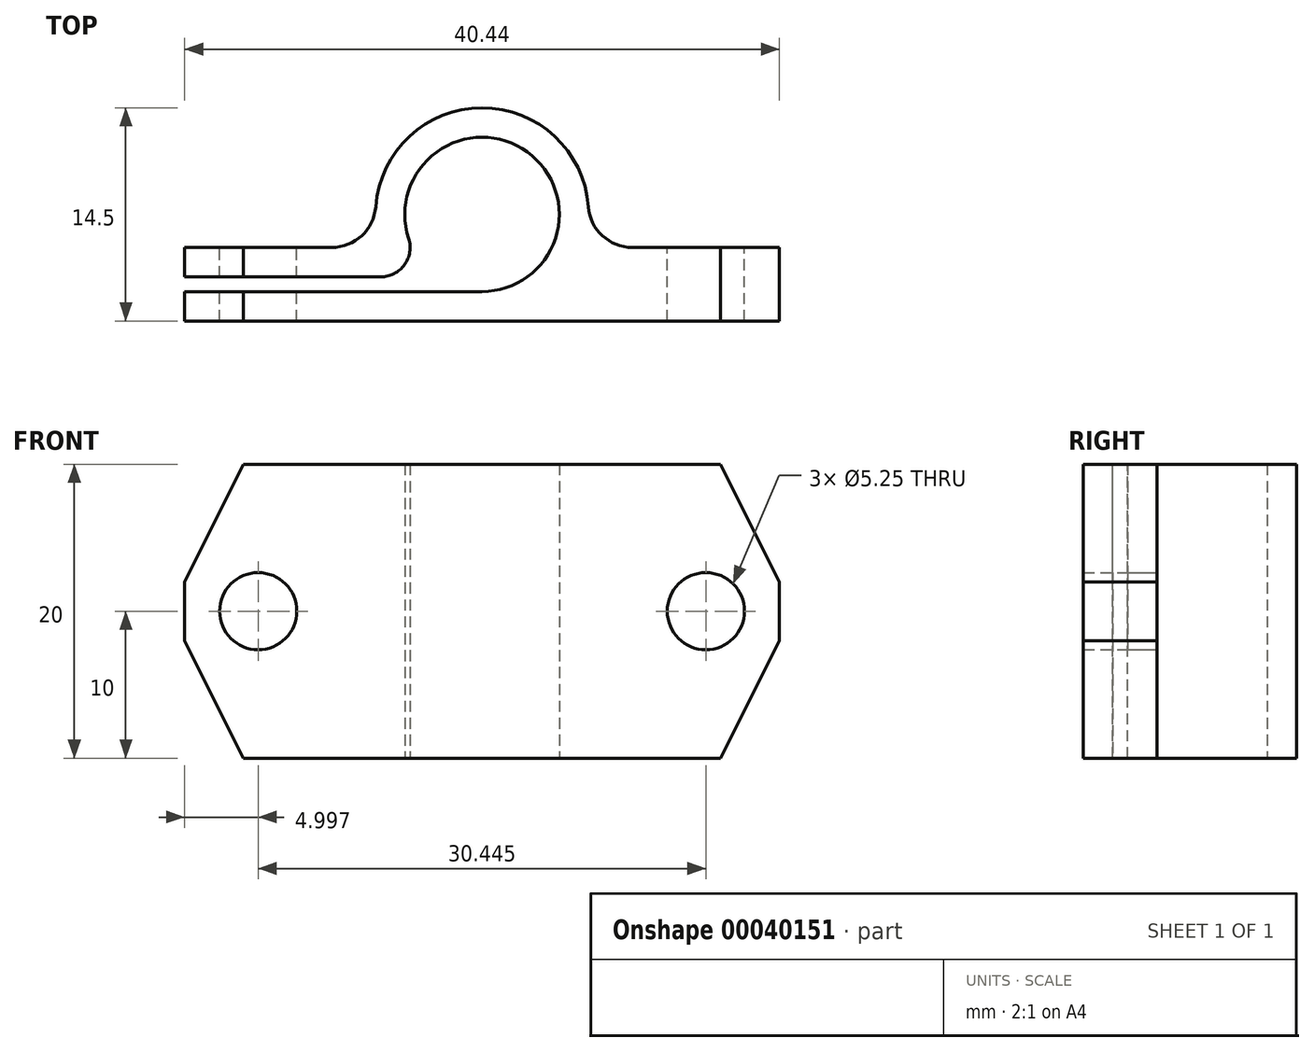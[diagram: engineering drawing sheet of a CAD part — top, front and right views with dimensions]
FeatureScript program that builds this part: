
annotation { "Feature Type Name" : "Feature", "Feature Type Description" : "" }
export const myFeature = defineFeature(function(context is Context, id is Id, definition is map)
    precondition{}
    {
        {
            var Q0;
            Q0=qCreatedBy(makeId("Top.planeOp"),FACE);
            var sketch = newSketch(context, id + "F0", { "sketchPlane" : qUnion([Q0])});
            skLineSegment(sketch, "E0", {"start": v(-20.22, 5) * mm, "end": v(-20.22, 0) * mm});
            skLineSegment(sketch, "E1", {"start": v(-20.22, 0) * mm, "end": v(20.22, 0) * mm});
            skLineSegment(sketch, "E2", {"start": v(20.22, 0) * mm, "end": v(20.22, 5) * mm});
            skLineSegment(sketch, "E3", {"start": v(20.22, 5) * mm, "end": v(10.22, 5) * mm});
            skLineSegment(sketch, "E4", {"start": v(-20.22, 5) * mm, "end": v(-10.22, 5) * mm});
            skArc(sketch, "E5", {"start": v(-7.23, 7.78) * mm, "mid": v(0, 14.5) * mm, "end": v(7.23, 7.78) * mm});
            skCircle(sketch, "E6", {"center": v(0, 7.25) * mm, "radius": 5.25 * mm});
            skPoint(sketch, "E7.visualSharp", {"position": v(-6.9, 5) * mm});
            skArc(sketch, "E7.filletArc", {"start": v(-10.22, 5) * mm, "mid": v(-8.18, 5.8) * mm, "end": v(-7.23, 7.78) * mm});
            skPoint(sketch, "E8.visualSharp", {"position": v(6.9, 5) * mm});
            skArc(sketch, "E8.filletArc", {"start": v(7.23, 7.78) * mm, "mid": v(8.18, 5.8) * mm, "end": v(10.22, 5) * mm});
            skSolve(sketch);
        }
        {
            var Q0;
            Q0 = qSketchRegion(id + "F0", true);
            extrude(context, id + "F1", {"entities" : qUnion([Q0]), "depth" : 20 * mm});
        }
        {
            var Q0;
            Q0=makeQuery(id+"F1.opExtrude","CAP_FACE",FACE,{"disambiguationData":[OSD([sQuery(id+"F0.wireOp",EDGE,"E0"),sQuery(id+"F0.wireOp",EDGE,"E1"),sQuery(id+"F0.wireOp",EDGE,"E2"),sQuery(id+"F0.wireOp",EDGE,"E3"),sQuery(id+"F0.wireOp",EDGE,"E4"),sQuery(id+"F0.wireOp",EDGE,"E5"),sQuery(id+"F0.wireOp",EDGE,"E6"),sQuery(id+"F0.wireOp",EDGE,"E7.filletArc"),sQuery(id+"F0.wireOp",EDGE,"E8.filletArc")])],"isStart":false});
            var sketch = newSketch(context, id + "F2", { "sketchPlane" : qUnion([Q0])});
            skLineSegment(sketch, "E9.bottom", {"start": v(0, 2) * mm, "end": v(-20.22, 2) * mm});
            skLineSegment(sketch, "E9.top", {"start": v(0, 3) * mm, "end": v(-20.22, 3) * mm});
            skLineSegment(sketch, "E9.left", {"start": v(0, 2) * mm, "end": v(0, 3) * mm});
            skLineSegment(sketch, "E9.right", {"start": v(-20.22, 2) * mm, "end": v(-20.22, 3) * mm});
            skSolve(sketch);
        }
        {
            var Q0;
            Q0 = qSketchRegion(id + "F2", true);
            extrude(context, id + "F3", {"entities" : qUnion([Q0]), "operationType" : NewBodyOperationType.REMOVE, "endBound" : BoundingType.THROUGH_ALL, "oppositeDirection" : true, "depth" : 25 * mm});
        }
        {
            var Q0;
            Q0=makeQuery(id+"F1.opExtrude","SWEPT_FACE",FACE,{"disambiguationData":[OSD([sQuery(id+"F0.wireOp",EDGE,"E3")])]});
            var sketch = newSketch(context, id + "F4", { "sketchPlane" : qUnion([Q0])});
            skCircle(sketch, "E10", {"center": v(-15.22, 10) * mm, "radius": 2.62 * mm});
            skPoint(sketch, "E10.centerSnap0", {"position": v(-20.22, 10) * mm});
            skPoint(sketch, "E10.centerSnap1", {"position": v(-15.22, 0) * mm});
            skCircle(sketch, "E11", {"center": v(15.22, 10) * mm, "radius": 2.62 * mm});
            skSolve(sketch);
        }
        {
            var Q0;
            Q0 = qSketchRegion(id + "F4", true);
            extrude(context, id + "F5", {"entities" : qUnion([Q0]), "operationType" : NewBodyOperationType.REMOVE, "endBound" : BoundingType.THROUGH_ALL, "oppositeDirection" : true, "depth" : 25 * mm});
        }
        {
            var Q0;
            {var subQ0=sQuery(id+"F0.wireOp",EDGE,"E0");var subQ1=sQuery(id+"F0.wireOp",EDGE,"E1");Q0=makeQuery(id+"F3.boolean.opBoolean","SPLIT",EDGE,{"disambiguationData":[TD([makeQuery(id+"F1.opExtrude","SWEPT_FACE",FACE,{"disambiguationData":[OSD([subQ1])]})])],"derivedFrom":makeQuery(id+"F1.opExtrude","CAP_EDGE",EDGE,{"disambiguationData":[OSD([subQ0])],"isStart":false})});}
            var Q1;
            {var subQ0=sQuery(id+"F0.wireOp",EDGE,"E0");var subQ1=sQuery(id+"F0.wireOp",EDGE,"E4");Q1=makeQuery(id+"F3.boolean.opBoolean","SPLIT",EDGE,{"disambiguationData":[TD([makeQuery(id+"F1.opExtrude","SWEPT_FACE",FACE,{"disambiguationData":[OSD([subQ1])]})])],"derivedFrom":makeQuery(id+"F1.opExtrude","CAP_EDGE",EDGE,{"disambiguationData":[OSD([subQ0])],"isStart":false})});}
            var Q2;
            Q2=makeQuery(id+"F1.opExtrude","CAP_EDGE",EDGE,{"disambiguationData":[OSD([sQuery(id+"F0.wireOp",EDGE,"E2")])],"isStart":false});
            var Q3;
            {var subQ0=sQuery(id+"F0.wireOp",EDGE,"E0");var subQ1=sQuery(id+"F0.wireOp",EDGE,"E1");Q3=makeQuery(id+"F3.boolean.opBoolean","SPLIT",EDGE,{"disambiguationData":[TD([makeQuery(id+"F1.opExtrude","SWEPT_FACE",FACE,{"disambiguationData":[OSD([subQ1])]})])],"derivedFrom":makeQuery(id+"F1.opExtrude","CAP_EDGE",EDGE,{"disambiguationData":[OSD([subQ0])],"isStart":true})});}
            chamfer(context, id + "F6", {"entities" : qUnion([Q0, Q1, Q2, Q3]), "chamferType" : ChamferType.TWO_OFFSETS, "width1" : 4 * mm, "oppositeDirection" : false, "width2" : 8 * mm, "tangentPropagation" : true});
        }
        {
            var Q0;
            Q0=makeQuery(id+"F1.opExtrude","CAP_EDGE",EDGE,{"disambiguationData":[OSD([sQuery(id+"F0.wireOp",EDGE,"E2")])],"isStart":true});
            var Q1;
            {var subQ0=sQuery(id+"F0.wireOp",EDGE,"E0");var subQ1=sQuery(id+"F0.wireOp",EDGE,"E4");Q1=makeQuery(id+"F3.boolean.opBoolean","SPLIT",EDGE,{"disambiguationData":[TD([makeQuery(id+"F1.opExtrude","SWEPT_FACE",FACE,{"disambiguationData":[OSD([subQ1])]})])],"derivedFrom":makeQuery(id+"F1.opExtrude","CAP_EDGE",EDGE,{"disambiguationData":[OSD([subQ0])],"isStart":true})});}
            chamfer(context, id + "F7", {"entities" : qUnion([Q0, Q1]), "chamferType" : ChamferType.TWO_OFFSETS, "width1" : 8 * mm, "oppositeDirection" : false, "width2" : 4 * mm, "tangentPropagation" : true});
        }
        {
            var Q0;
            Q0=makeQuery(id+"F3.boolean.opBoolean","INTERSECT",EDGE,{"derivedFrom":[makeQuery(id+"F1.opExtrude","SWEPT_FACE",FACE,{"disambiguationData":[OSD([sQuery(id+"F0.wireOp",EDGE,"E6")])]}),makeQuery(id+"F3.opExtrude","SWEPT_FACE",FACE,{"disambiguationData":[OSD([sQuery(id+"F2.wireOp",EDGE,"E9.top")])]})]});
            fillet(context, id + "F8", {"entities" : qUnion([Q0]), "radius" : 2 * mm, "tangentPropagation" : true, "allowEdgeOverflow" : false});
        }
    });
